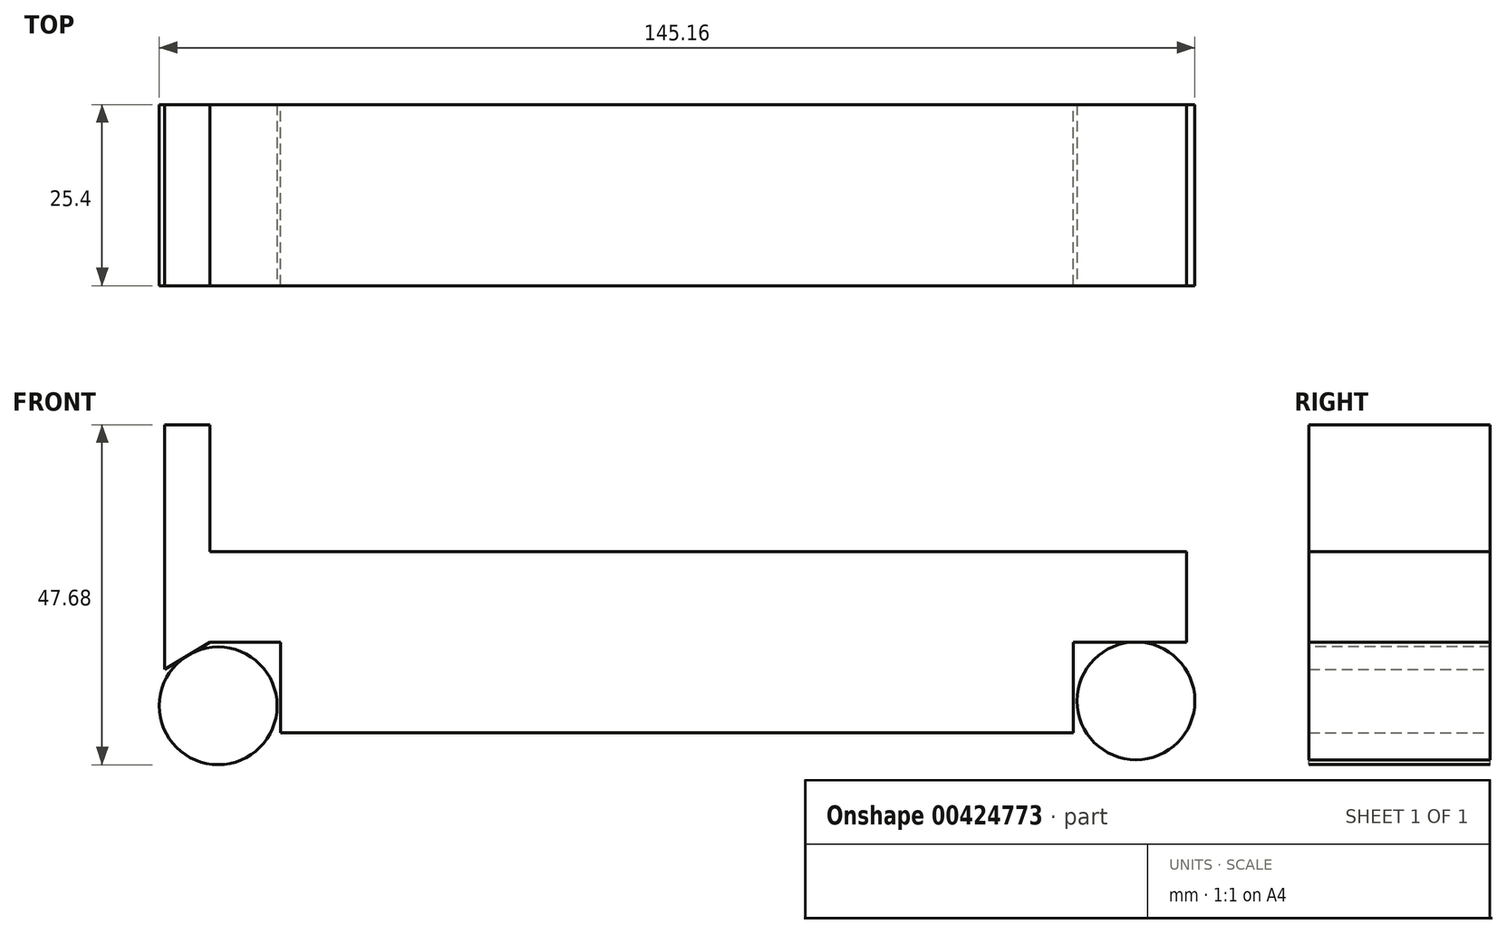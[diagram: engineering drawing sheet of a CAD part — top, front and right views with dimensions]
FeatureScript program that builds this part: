
annotation { "Feature Type Name" : "Feature", "Feature Type Description" : "" }
export const myFeature = defineFeature(function(context is Context, id is Id, definition is map)
    precondition{}
    {
        {
            var Q0;
            Q0=qCreatedBy(makeId("Front.planeOp"),FACE);
            var sketch = newSketch(context, id + "F0", { "sketchPlane" : qUnion([Q0])});
            skLineSegment(sketch, "E0", {"start": v(0, 0) * mm, "end": v(136.9, 0) * mm});
            skLineSegment(sketch, "E1", {"start": v(136.9, 0) * mm, "end": v(136.9, -12.7) * mm});
            skLineSegment(sketch, "E2", {"start": v(136.9, -12.7) * mm, "end": v(121.03, -12.7) * mm});
            skLineSegment(sketch, "E3", {"start": v(121.03, -12.7) * mm, "end": v(121.03, -25.4) * mm});
            skLineSegment(sketch, "E4", {"start": v(121.03, -25.4) * mm, "end": v(9.9, -25.4) * mm});
            skLineSegment(sketch, "E5", {"start": v(9.9, -25.4) * mm, "end": v(9.9, -12.7) * mm});
            skLineSegment(sketch, "E6", {"start": v(9.9, -12.7) * mm, "end": v(0, -12.7) * mm});
            skLineSegment(sketch, "E7", {"start": v(0, -12.7) * mm, "end": v(0, 0) * mm});
            skSolve(sketch);
        }
        {
            var Q0;
            Q0 = qSketchRegion(id + "F0", true);
            extrude(context, id + "F1", {"entities" : qUnion([Q0]), "depth" : 25.4 * mm});
        }
        {
            var Q0;
            Q0=qCreatedBy(makeId("Front.planeOp"),FACE);
            var sketch = newSketch(context, id + "F2", { "sketchPlane" : qUnion([Q0])});
            skLineSegment(sketch, "E8", {"start": v(0, -12.7) * mm, "end": v(0, 17.78) * mm});
            skLineSegment(sketch, "E9", {"start": v(0, 17.78) * mm, "end": v(-6.35, 17.78) * mm});
            skLineSegment(sketch, "E10", {"start": v(-6.35, 17.78) * mm, "end": v(-6.35, -16.51) * mm});
            skLineSegment(sketch, "E11", {"start": v(-6.35, -16.51) * mm, "end": v(0, -12.7) * mm});
            skSolve(sketch);
        }
        {
            var Q0;
            Q0 = qSketchRegion(id + "F2", true);
            extrude(context, id + "F3", {"entities" : qUnion([Q0]), "operationType" : NewBodyOperationType.ADD, "depth" : 25.4 * mm});
        }
        {
            var Q0;
            Q0=makeQuery(id+"F3.boolean.opBoolean","MERGE",FACE,{"derivedFrom":[makeQuery(id+"F1.opExtrude","CAP_FACE",FACE,{"disambiguationData":[OSD([sQuery(id+"F0.wireOp",EDGE,"E0"),sQuery(id+"F0.wireOp",EDGE,"E1"),sQuery(id+"F0.wireOp",EDGE,"E2"),sQuery(id+"F0.wireOp",EDGE,"E3"),sQuery(id+"F0.wireOp",EDGE,"E4"),sQuery(id+"F0.wireOp",EDGE,"E5"),sQuery(id+"F0.wireOp",EDGE,"E6"),sQuery(id+"F0.wireOp",EDGE,"E7")])],"isStart":false}),makeQuery(id+"F3.opExtrude","CAP_FACE",FACE,{"disambiguationData":[OSD([sQuery(id+"F2.wireOp",EDGE,"E8"),sQuery(id+"F2.wireOp",EDGE,"E9"),sQuery(id+"F2.wireOp",EDGE,"E10"),sQuery(id+"F2.wireOp",EDGE,"E11")])],"isStart":false})]});
            var sketch = newSketch(context, id + "F4", { "sketchPlane" : qUnion([Q0])});
            skCircle(sketch, "E12", {"center": v(1.14, -21.64) * mm, "radius": 8.26 * mm});
            skSolve(sketch);
        }
        {
            var Q0;
            Q0 = qSketchRegion(id + "F4", true);
            extrude(context, id + "F5", {"entities" : qUnion([Q0]), "oppositeDirection" : true, "depth" : 25.4 * mm});
        }
        {
            var Q0;
            Q0=makeQuery(id+"F3.boolean.opBoolean","MERGE",FACE,{"derivedFrom":[makeQuery(id+"F1.opExtrude","CAP_FACE",FACE,{"disambiguationData":[OSD([sQuery(id+"F0.wireOp",EDGE,"E0"),sQuery(id+"F0.wireOp",EDGE,"E1"),sQuery(id+"F0.wireOp",EDGE,"E2"),sQuery(id+"F0.wireOp",EDGE,"E3"),sQuery(id+"F0.wireOp",EDGE,"E4"),sQuery(id+"F0.wireOp",EDGE,"E5"),sQuery(id+"F0.wireOp",EDGE,"E6"),sQuery(id+"F0.wireOp",EDGE,"E7")])],"isStart":false}),makeQuery(id+"F3.opExtrude","CAP_FACE",FACE,{"disambiguationData":[OSD([sQuery(id+"F2.wireOp",EDGE,"E8"),sQuery(id+"F2.wireOp",EDGE,"E9"),sQuery(id+"F2.wireOp",EDGE,"E10"),sQuery(id+"F2.wireOp",EDGE,"E11")])],"isStart":false})]});
            var sketch = newSketch(context, id + "F6", { "sketchPlane" : qUnion([Q0])});
            skCircle(sketch, "E13", {"center": v(129.8, -20.96) * mm, "radius": 8.26 * mm});
            skSolve(sketch);
        }
        {
            var Q0;
            Q0 = qSketchRegion(id + "F6", true);
            extrude(context, id + "F7", {"entities" : qUnion([Q0]), "oppositeDirection" : true, "depth" : 25.4 * mm});
        }
    });
